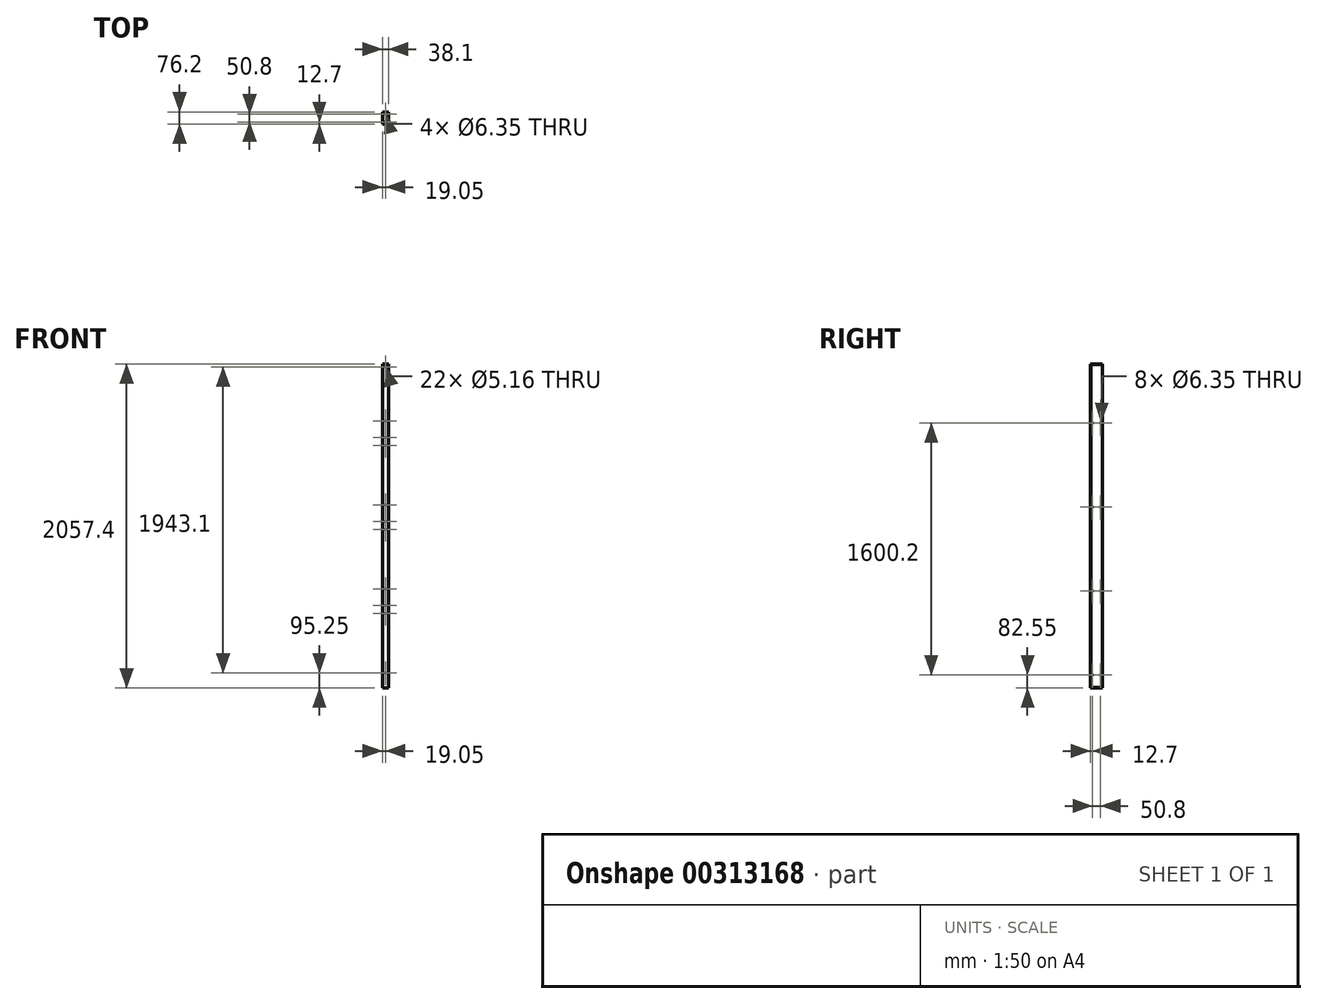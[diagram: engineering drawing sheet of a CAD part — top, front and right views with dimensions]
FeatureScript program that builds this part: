
annotation { "Feature Type Name" : "Feature", "Feature Type Description" : "" }
export const myFeature = defineFeature(function(context is Context, id is Id, definition is map)
    precondition{}
    {
        {
            var Q0;
            Q0=qCreatedBy(makeId("Top.planeOp"),FACE);
            var sketch = newSketch(context, id + "F0", { "sketchPlane" : qUnion([Q0])});
            skLineSegment(sketch, "E0.bottom", {"start": v(0, 0) * mm, "end": v(38.1, 0) * mm});
            skLineSegment(sketch, "E0.top", {"start": v(0, 76.2) * mm, "end": v(38.1, 76.2) * mm});
            skLineSegment(sketch, "E0.left", {"start": v(0, 0) * mm, "end": v(0, 76.2) * mm});
            skLineSegment(sketch, "E0.right", {"start": v(38.1, 0) * mm, "end": v(38.1, 76.2) * mm});
            skSolve(sketch);
        }
        {
            var Q0;
            Q0=qSketchRegion(id+"F0",true);
            extrude(context, id + "F1", {"entities" : qUnion([Q0]), "endBound" : BoundingType.SYMMETRIC, "depth" : 2057.4 * mm});
        }
        {
            var Q0;
            Q0=makeQuery(id+"F1.opExtrude","SWEPT_FACE",FACE,{"disambiguationData":[OSD([sQuery(id+"F0.wireOp",EDGE,"E0.right")])]});
            shell(context, id + "F2", {"entities" : qUnion([Q0]), "thickness" : 2.78 * mm});
        }
        {
            var Q0;
            Q0=makeQuery(id+"F1.opExtrude","SWEPT_FACE",FACE,{"disambiguationData":[OSD([sQuery(id+"F0.wireOp",EDGE,"E0.left")])]});
            var sketch = newSketch(context, id + "F3", { "sketchPlane" : qUnion([Q0])});
            skCircle(sketch, "E1", {"center": v(-63.5, -946.15) * mm, "radius": 3.18 * mm});
            skCircle(sketch, "E2", {"center": v(-12.7, -946.15) * mm, "radius": 3.18 * mm});
            skCircle(sketch, "E3.0.1.0", {"center": v(-63.5, -412.75) * mm, "radius": 3.18 * mm});
            skCircle(sketch, "E3.0.1.1", {"center": v(-12.7, -412.75) * mm, "radius": 3.18 * mm});
            skCircle(sketch, "E3.0.2.0", {"center": v(-63.5, 120.65) * mm, "radius": 3.18 * mm});
            skCircle(sketch, "E3.0.2.1", {"center": v(-12.7, 120.65) * mm, "radius": 3.18 * mm});
            skCircle(sketch, "E3.0.3.0", {"center": v(-63.5, 654.05) * mm, "radius": 3.18 * mm});
            skCircle(sketch, "E3.0.3.1", {"center": v(-12.7, 654.05) * mm, "radius": 3.18 * mm});
            skLineSegment(sketch, "E3.direction1", {"start": v(-63.5, -946.15) * mm, "end": v(-12.7, -946.15) * mm, "construction": true});
            skLineSegment(sketch, "E3.direction2", {"start": v(-63.5, -946.15) * mm, "end": v(-63.5, -412.75) * mm, "construction": true});
            skSolve(sketch);
        }
        {
            var Q0;
            Q0 = qSketchRegion(id + "F3", true);
            extrude(context, id + "F4", {"entities" : qUnion([Q0]), "operationType" : NewBodyOperationType.REMOVE, "endBound" : BoundingType.THROUGH_ALL, "oppositeDirection" : true, "depth" : 25.4 * mm});
        }
        {
            var Q0;
            Q0=makeQuery(id+"F1.opExtrude","CAP_FACE",FACE,{"disambiguationData":[OSD([sQuery(id+"F0.wireOp",EDGE,"E0.bottom"),sQuery(id+"F0.wireOp",EDGE,"E0.top"),sQuery(id+"F0.wireOp",EDGE,"E0.left"),sQuery(id+"F0.wireOp",EDGE,"E0.right")])],"isStart":true});
            var sketch = newSketch(context, id + "F5", { "sketchPlane" : qUnion([Q0])});
            skCircle(sketch, "E4", {"center": v(19.05, -12.7) * mm, "radius": 3.18 * mm});
            skPoint(sketch, "E4.centerSnap0", {"position": v(19.05, 0) * mm});
            skCircle(sketch, "E5", {"center": v(19.05, -63.5) * mm, "radius": 3.18 * mm});
            skSolve(sketch);
        }
        {
            var Q0;
            Q0 = qSketchRegion(id + "F5", true);
            extrude(context, id + "F6", {"entities" : qUnion([Q0]), "operationType" : NewBodyOperationType.REMOVE, "endBound" : BoundingType.THROUGH_ALL, "oppositeDirection" : true, "depth" : 25.4 * mm});
        }
        {
            var Q0;
            Q0=makeQuery(id+"F1.opExtrude","SWEPT_FACE",FACE,{"disambiguationData":[OSD([sQuery(id+"F0.wireOp",EDGE,"E0.top")])]});
            var sketch = newSketch(context, id + "F7", { "sketchPlane" : qUnion([Q0])});
            skCircle(sketch, "E6", {"center": v(-19.05, 561.98) * mm, "radius": 2.58 * mm});
            skCircle(sketch, "E7", {"center": v(-19.05, 511.18) * mm, "radius": 2.58 * mm});
            skCircle(sketch, "E8", {"center": v(-19.05, 133.35) * mm, "radius": 2.58 * mm});
            skCircle(sketch, "E9.0.1.0", {"center": v(-19.05, -22.22) * mm, "radius": 2.58 * mm});
            skCircle(sketch, "E9.0.1.1", {"center": v(-19.05, 28.58) * mm, "radius": 2.58 * mm});
            skCircle(sketch, "E9.0.1.2", {"center": v(-19.05, -400.05) * mm, "radius": 2.58 * mm});
            skCircle(sketch, "E9.0.2.0", {"center": v(-19.05, -555.62) * mm, "radius": 2.58 * mm});
            skCircle(sketch, "E9.0.2.1", {"center": v(-19.05, -504.83) * mm, "radius": 2.58 * mm});
            skCircle(sketch, "E9.0.2.2", {"center": v(-19.05, -933.45) * mm, "radius": 2.58 * mm});
            skLineSegment(sketch, "E9.direction1", {"start": v(-19.05, 133.35) * mm, "end": v(0, 133.35) * mm, "construction": true});
            skLineSegment(sketch, "E9.direction2", {"start": v(-19.05, 133.35) * mm, "end": v(-19.05, -400.05) * mm, "construction": true});
            skCircle(sketch, "E10", {"center": v(-19.05, 666.75) * mm, "radius": 2.58 * mm});
            skCircle(sketch, "E11", {"center": v(-19.05, 1009.65) * mm, "radius": 2.58 * mm});
            skSolve(sketch);
        }
        {
            var Q0;
            Q0 = qSketchRegion(id + "F7", true);
            extrude(context, id + "F8", {"entities" : qUnion([Q0]), "operationType" : NewBodyOperationType.REMOVE, "endBound" : BoundingType.THROUGH_ALL, "oppositeDirection" : true, "depth" : 25.4 * mm});
        }
    });
